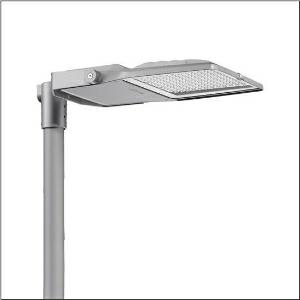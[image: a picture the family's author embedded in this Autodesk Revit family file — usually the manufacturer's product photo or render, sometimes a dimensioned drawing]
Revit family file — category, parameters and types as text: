
# Revit family: floodlight_fl_21_iq_midi___pl43_5xa7782e4a3a_f2c8
name_source: partatom
category: Lighting Fixtures
units: mm (PartAtom-declared; Revit-internal decimal feet)

## family parameters
Cut with Voids When Loaded = No
Host = Face
Light Source = No
Part Type = Normal
Room Calculation Point = No
Round Connector Dimension = Use Diameter
Shared = No

## types (1)
- --- (1 x LED, 28730 lm, 208.1 W, 4000K)
    Apparent Load = 208 VA
    CIE Flux Codes = 27 78 99 100 100
    Color Rendering = 70
    Color Temperature = 4000K
    Default Elevation = 1800 mm
    Description = Floodlight FL 21 iQ midi, floodlight, primary light control with lens, of PMMA, primary optical cover: protective disc, of toughened safety glass, transparent, light distribution: PL43, light emission: direct distribution, installation type: surface-mounted, LED, High Power LED, rated luminous flux: 28.730lm, luminous efficacy: 138lm/W, light colour: 740, colour temperature: 4000K, control gear: iQ Street-Remote/DALI, control: optimised constant luminous flux control (CLO 2.0), Desk-Remote (wireless, voltage-free reading and setting of iQ features in the workshop via application-optimized NFC function/RFID function), Smart-Wire, Night-Set, Temp-Guard, Auto-Match, Street-Remote, with terminal, 6-pole, mains connection: 220..240V, AC, 50/60Hz, start of lifetime: 208W, end of service life: 227W, reduction: 90W, luminaire housing, of diecast aluminium, powder-coated, Siteco® metallic grey (DB 702S), corrosivity category C5 mid according to DIN EN ISO 12944, suitable for swimming pools, chlorine-resistant, sealing non-destructively replaceable, please order mast flange separately, mast bracket, of steel, galvanised, powder-coated, Siteco® metallic grey (DB 702S), protection rating (complete): IP66, insulation class (complete): insulation class II (safety insulation), certification: CE, ENEC, VDE, protection symbol: D, impact resistance: IK08, permissible operating ambient temperature: -40..+40°C, permissible operating ambient temperature for outdoor applications: -40..+50°C, standard: DIN EN 12944, LABS conformity tested according to VDMA 24364:2018-05, packaging unit: 1 piece

Light Distribution: PL43
    Height = 76 mm
    Lamp = 1 x LED
    Lamp Light Flux = 28730 lm
    Lamp Power = 208.1 W
    Lamp count = 1
    Length = 657 mm
    Luminous efficacy = 138 lm/W
    Manufacturer = Siteco
    ModVariant = No
    Model = 5XA7782E4A3A
    Number of Poles = 1
    OnlyDefault = Yes
    Power Factor = 1
    Product Name = Floodlight FL 21 iQ midi | PL43
    Product group = floodlight | pylon annexe
    ProductGroupID = 6200
    Protection Class = Protection class II
    Protection Degree = IP 66
    RLX_Detail_Level = 1
    RLX_Emergency_Light_Flux = 0 lm
    RLX_Emergency_Type = 0
    RLX_Emergency_Type_DB = No
    RlxData = <blob elided: 153481 chars, md5=65f1eb6e>
    Socket = socket
    Standby Power = 0 W
    System Light Flux = 28730 lm
    System Power = 208 W
    Type Comments = factory setting: luminous flux: 100 % | dim-lin: 254 | 710 mA
    Type Image = l_1007123.jpg
    URL = http://relux.com
    VarID = @adj_105072
    Voltage = 0 V
    Weight = 0.00 kg
    Width = 442 mm

## geometry (parser evidence)
native form markers: Blend x4, Sweep x15
no freeform markers — native parametric forms only
